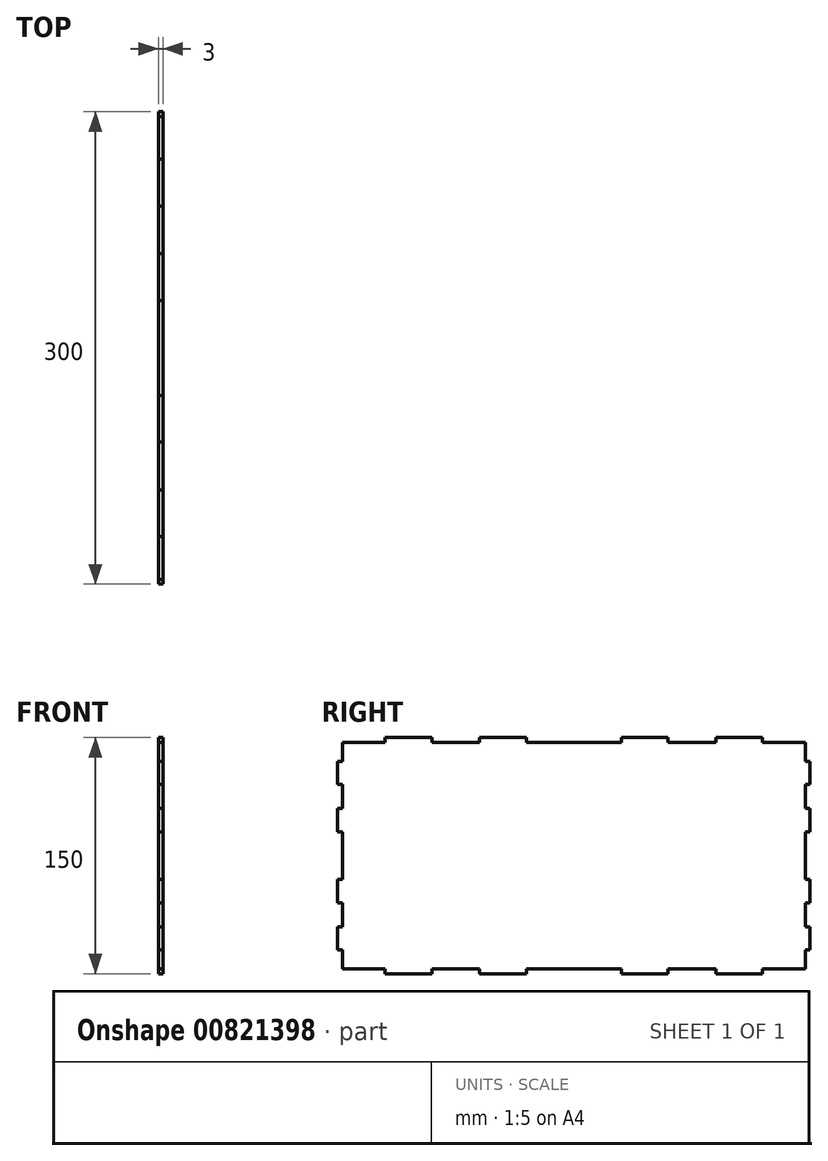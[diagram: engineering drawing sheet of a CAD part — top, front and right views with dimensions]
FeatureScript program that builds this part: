
annotation { "Feature Type Name" : "Feature", "Feature Type Description" : "" }
export const myFeature = defineFeature(function(context is Context, id is Id, definition is map)
    precondition{}
    {
        {
            var Q0;
            Q0=qCreatedBy(makeId("Right.planeOp"),FACE);
            var sketch = newSketch(context, id + "F0", { "sketchPlane" : qUnion([Q0])});
            skPoint(sketch, "E0.middle", {"position": v(0, 0) * mm});
            skLineSegment(sketch, "E1", {"start": v(-119.88, -75) * mm, "end": v(-119.88, -72) * mm});
            skLineSegment(sketch, "E2", {"start": v(-119.88, -75) * mm, "end": v(-90.13, -75) * mm});
            skLineSegment(sketch, "E3", {"start": v(-90.13, -75) * mm, "end": v(-90.13, -72) * mm});
            skLineSegment(sketch, "E4", {"start": v(-90.13, -72) * mm, "end": v(-59.88, -72) * mm});
            skLineSegment(sketch, "E5", {"start": v(-59.88, -72) * mm, "end": v(-59.88, -75) * mm});
            skLineSegment(sketch, "E6", {"start": v(-59.88, -75) * mm, "end": v(-30.13, -75) * mm});
            skLineSegment(sketch, "E7", {"start": v(-30.13, -75) * mm, "end": v(-30.13, -72) * mm});
            skLineSegment(sketch, "E8", {"start": v(-30.13, -72) * mm, "end": v(0, -72) * mm});
            skLineSegment(sketch, "E9.MirrorCS", {"start": v(119.88, -75) * mm, "end": v(119.88, -72) * mm});
            skLineSegment(sketch, "E10.MirrorCS", {"start": v(30.13, -75) * mm, "end": v(30.13, -72) * mm});
            skLineSegment(sketch, "E11.MirrorCS", {"start": v(59.88, -72) * mm, "end": v(59.88, -75) * mm});
            skLineSegment(sketch, "E12.MirrorCS", {"start": v(90.13, -75) * mm, "end": v(90.13, -72) * mm});
            skLineSegment(sketch, "E13.MirrorCS", {"start": v(30.13, -72) * mm, "end": v(0, -72) * mm});
            skLineSegment(sketch, "E14.MirrorCS", {"start": v(119.88, -72) * mm, "end": v(150, -72) * mm});
            skLineSegment(sketch, "E15.MirrorCS", {"start": v(59.88, -75) * mm, "end": v(30.13, -75) * mm});
            skLineSegment(sketch, "E16.MirrorCS", {"start": v(119.88, -75) * mm, "end": v(90.13, -75) * mm});
            skLineSegment(sketch, "E17.MirrorCS", {"start": v(90.13, -72) * mm, "end": v(59.88, -72) * mm});
            skLineSegment(sketch, "E18.MirrorCS", {"start": v(59.88, 72) * mm, "end": v(59.88, 75) * mm});
            skLineSegment(sketch, "E19.MirrorCS", {"start": v(90.13, 75) * mm, "end": v(90.13, 72) * mm});
            skLineSegment(sketch, "E20.MirrorCS", {"start": v(30.13, 75) * mm, "end": v(30.13, 72) * mm});
            skLineSegment(sketch, "E21.MirrorCS", {"start": v(-59.88, 72) * mm, "end": v(-59.88, 75) * mm});
            skLineSegment(sketch, "E22.MirrorCS", {"start": v(-119.88, 75) * mm, "end": v(-119.88, 72) * mm});
            skLineSegment(sketch, "E23.MirrorCS", {"start": v(119.88, 75) * mm, "end": v(119.88, 72) * mm});
            skLineSegment(sketch, "E24.MirrorCS", {"start": v(-90.13, 75) * mm, "end": v(-90.13, 72) * mm});
            skLineSegment(sketch, "E25.MirrorCS", {"start": v(-30.13, 75) * mm, "end": v(-30.13, 72) * mm});
            skLineSegment(sketch, "E26.MirrorCS", {"start": v(90.13, 72) * mm, "end": v(59.88, 72) * mm});
            skLineSegment(sketch, "E27.MirrorCS", {"start": v(59.88, 75) * mm, "end": v(30.13, 75) * mm});
            skLineSegment(sketch, "E28.MirrorCS", {"start": v(30.13, 72) * mm, "end": v(0, 72) * mm});
            skLineSegment(sketch, "E29.MirrorCS", {"start": v(-90.13, 72) * mm, "end": v(-59.88, 72) * mm});
            skLineSegment(sketch, "E30.MirrorCS", {"start": v(-119.88, 75) * mm, "end": v(-90.13, 75) * mm});
            skLineSegment(sketch, "E31.MirrorCS", {"start": v(119.88, 75) * mm, "end": v(90.13, 75) * mm});
            skLineSegment(sketch, "E32.MirrorCS", {"start": v(-59.88, 75) * mm, "end": v(-30.13, 75) * mm});
            skLineSegment(sketch, "E33.MirrorCS", {"start": v(-30.13, 72) * mm, "end": v(0, 72) * mm});
            skLineSegment(sketch, "E34", {"start": v(-150, -59.88) * mm, "end": v(-147, -59.88) * mm});
            skLineSegment(sketch, "E35", {"start": v(-147, -59.88) * mm, "end": v(-147, -72) * mm});
            skLineSegment(sketch, "E36", {"start": v(-150, -59.88) * mm, "end": v(-150, -45.13) * mm});
            skLineSegment(sketch, "E37", {"start": v(-150, -45.13) * mm, "end": v(-147, -45.13) * mm});
            skLineSegment(sketch, "E38", {"start": v(-147, -45.13) * mm, "end": v(-147, -29.88) * mm});
            skLineSegment(sketch, "E39", {"start": v(-147, -29.88) * mm, "end": v(-150, -29.88) * mm});
            skLineSegment(sketch, "E40", {"start": v(-150, -29.88) * mm, "end": v(-150, -15.13) * mm});
            skLineSegment(sketch, "E41", {"start": v(-150, -15.13) * mm, "end": v(-147, -15.13) * mm});
            skLineSegment(sketch, "E42", {"start": v(-147, -72) * mm, "end": v(-119.88, -72) * mm});
            skLineSegment(sketch, "E43.MirrorCS", {"start": v(-150, 59.88) * mm, "end": v(-147, 59.88) * mm});
            skLineSegment(sketch, "E44.MirrorCS", {"start": v(-150, 15.13) * mm, "end": v(-147, 15.13) * mm});
            skLineSegment(sketch, "E45.MirrorCS", {"start": v(-147, 29.88) * mm, "end": v(-150, 29.88) * mm});
            skLineSegment(sketch, "E46.MirrorCS", {"start": v(-150, 45.13) * mm, "end": v(-147, 45.13) * mm});
            skLineSegment(sketch, "E47.MirrorCS", {"start": v(-147, 59.88) * mm, "end": v(-147, 72) * mm});
            skLineSegment(sketch, "E48.MirrorCS", {"start": v(-150, 59.88) * mm, "end": v(-150, 45.13) * mm});
            skLineSegment(sketch, "E49.MirrorCS", {"start": v(-150, 29.88) * mm, "end": v(-150, 15.13) * mm});
            skLineSegment(sketch, "E50.MirrorCS", {"start": v(-147, 45.13) * mm, "end": v(-147, 29.88) * mm});
            skLineSegment(sketch, "E51.MirrorCS", {"start": v(150, -15.13) * mm, "end": v(147, -15.13) * mm});
            skLineSegment(sketch, "E52.MirrorCS", {"start": v(150, -59.88) * mm, "end": v(147, -59.88) * mm});
            skLineSegment(sketch, "E53.MirrorCS", {"start": v(147, 29.88) * mm, "end": v(150, 29.88) * mm});
            skLineSegment(sketch, "E54.MirrorCS", {"start": v(150, 59.88) * mm, "end": v(147, 59.88) * mm});
            skLineSegment(sketch, "E55.MirrorCS", {"start": v(150, 45.13) * mm, "end": v(147, 45.13) * mm});
            skLineSegment(sketch, "E56.MirrorCS", {"start": v(147, -29.88) * mm, "end": v(150, -29.88) * mm});
            skLineSegment(sketch, "E57.MirrorCS", {"start": v(150, -45.13) * mm, "end": v(147, -45.13) * mm});
            skLineSegment(sketch, "E58.MirrorCS", {"start": v(150, 15.13) * mm, "end": v(147, 15.13) * mm});
            skLineSegment(sketch, "E59.MirrorCS", {"start": v(150, -29.88) * mm, "end": v(150, -15.13) * mm});
            skLineSegment(sketch, "E60.MirrorCS", {"start": v(150, 59.88) * mm, "end": v(150, 45.13) * mm});
            skLineSegment(sketch, "E61.MirrorCS", {"start": v(150, 29.88) * mm, "end": v(150, 15.13) * mm});
            skLineSegment(sketch, "E62.MirrorCS", {"start": v(147, -59.88) * mm, "end": v(147, -72) * mm});
            skLineSegment(sketch, "E63.MirrorCS", {"start": v(147, -45.13) * mm, "end": v(147, -29.88) * mm});
            skLineSegment(sketch, "E64.MirrorCS", {"start": v(150, -59.88) * mm, "end": v(150, -45.13) * mm});
            skLineSegment(sketch, "E65.MirrorCS", {"start": v(147, 59.88) * mm, "end": v(147, 72) * mm});
            skLineSegment(sketch, "E66.MirrorCS", {"start": v(147, 45.13) * mm, "end": v(147, 29.88) * mm});
            skLineSegment(sketch, "E67", {"start": v(-147, 72) * mm, "end": v(-119.88, 72) * mm});
            skLineSegment(sketch, "E68", {"start": v(147, 72) * mm, "end": v(119.88, 72) * mm});
            skLineSegment(sketch, "E69", {"start": v(147, 15.13) * mm, "end": v(147, -15.13) * mm});
            skLineSegment(sketch, "E70", {"start": v(-147, 15.13) * mm, "end": v(-147, -15.13) * mm});
            skSolve(sketch);
        }
        {
            var Q0;
            Q0=makeQuery(id+"F0.imprint","IMPRINT",FACE,{"disambiguationData":[TD([[makeQuery(id+"F0.imprint","IMPRINT",EDGE,{"derivedFrom":sQuery(id+"F0.wireOp",EDGE,"E1")}),-1.0]])]});
            extrude(context, id + "F1", {"entities" : qUnion([Q0]), "depth" : 3 * mm, "offsetDistance" : 25 * mm});
        }
    });
